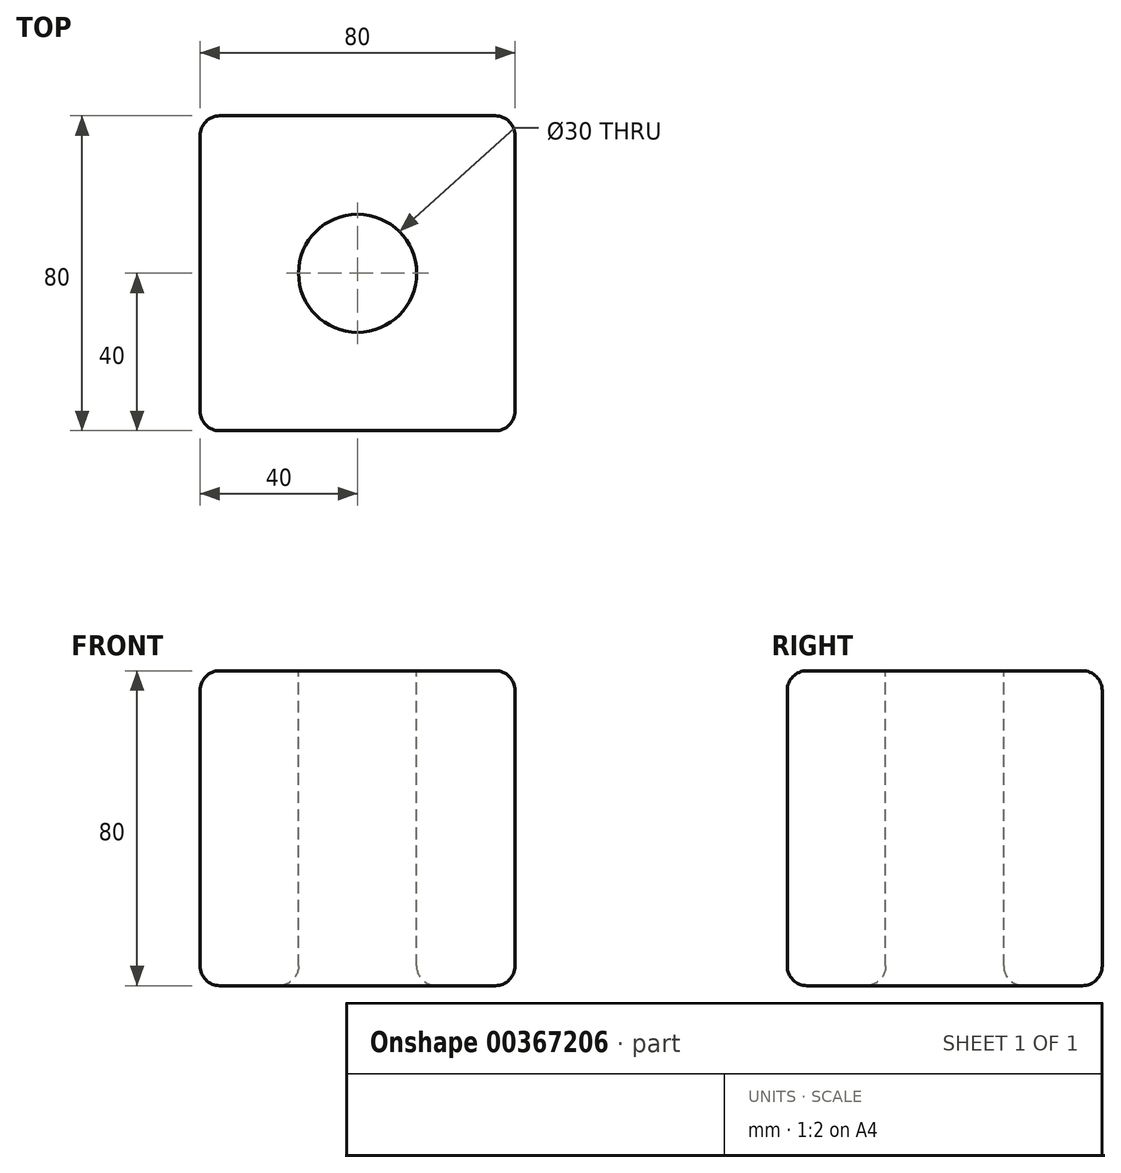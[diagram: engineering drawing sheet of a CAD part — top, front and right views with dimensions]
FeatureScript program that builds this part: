
annotation { "Feature Type Name" : "Feature", "Feature Type Description" : "" }
export const myFeature = defineFeature(function(context is Context, id is Id, definition is map)
    precondition{}
    {
        {
            var Q0;
            Q0=qCreatedBy(makeId("Top.planeOp"),FACE);
            var sketch = newSketch(context, id + "F0", { "sketchPlane" : qUnion([Q0])});
            skLineSegment(sketch, "E0.bottom", {"start": v(-40, 40) * mm, "end": v(40, 40) * mm});
            skLineSegment(sketch, "E0.top", {"start": v(-40, -40) * mm, "end": v(40, -40) * mm});
            skLineSegment(sketch, "E0.left", {"start": v(-40, 40) * mm, "end": v(-40, -40) * mm});
            skLineSegment(sketch, "E0.right", {"start": v(40, 40) * mm, "end": v(40, -40) * mm});
            skPoint(sketch, "E0.middle", {"position": v(0, 0) * mm});
            skSolve(sketch);
        }
        {
            var Q0;
            Q0=makeQuery(id+"F0.imprint","IMPRINT",FACE,{"disambiguationData":[TD([[makeQuery(id+"F0.imprint","IMPRINT",EDGE,{"derivedFrom":sQuery(id+"F0.wireOp",EDGE,"E0.bottom")}),-1.0]])]});
            extrude(context, id + "F1", {"entities" : qUnion([Q0]), "depth" : 80 * mm});
        }
        {
            var Q0;
            Q0=makeQuery(id+"F1.opExtrude","CAP_FACE",FACE,{"disambiguationData":[OSD([sQuery(id+"F0.wireOp",EDGE,"E0.bottom"),sQuery(id+"F0.wireOp",EDGE,"E0.top"),sQuery(id+"F0.wireOp",EDGE,"E0.left"),sQuery(id+"F0.wireOp",EDGE,"E0.right")])],"isStart":false});
            var sketch = newSketch(context, id + "F2", { "sketchPlane" : qUnion([Q0])});
            skCircle(sketch, "E1", {"center": v(0, 0) * mm, "radius": 15 * mm});
            skSolve(sketch);
        }
        {
            var Q0;
            Q0=makeQuery(id+"F2.imprint","IMPRINT",FACE,{"disambiguationData":[TD([[makeQuery(id+"F2.imprint","IMPRINT",EDGE,{"derivedFrom":sQuery(id+"F2.wireOp",EDGE,"E1")}),1.0]])]});
            extrude(context, id + "F3", {"entities" : qUnion([Q0]), "operationType" : NewBodyOperationType.REMOVE, "endBound" : BoundingType.THROUGH_ALL, "oppositeDirection" : true, "depth" : 25 * mm});
        }
        {
            var Q0;
            Q0=makeQuery(id+"F1.opExtrude","SWEPT_EDGE",EDGE,{"disambiguationData":[OSD([sQuery(id+"F0.wireOp",EDGE,"E0.bottom"),sQuery(id+"F0.wireOp",EDGE,"E0.left")])]});
            var Q1;
            Q1=makeQuery(id+"F1.opExtrude","SWEPT_FACE",FACE,{"disambiguationData":[OSD([sQuery(id+"F0.wireOp",EDGE,"E0.bottom")])]});
            var Q2;
            Q2=makeQuery(id+"F1.opExtrude","SWEPT_EDGE",EDGE,{"disambiguationData":[OSD([sQuery(id+"F0.wireOp",EDGE,"E0.bottom"),sQuery(id+"F0.wireOp",EDGE,"E0.right")])]});
            var Q3;
            Q3=makeQuery(id+"F1.opExtrude","SWEPT_FACE",FACE,{"disambiguationData":[OSD([sQuery(id+"F0.wireOp",EDGE,"E0.left")])]});
            var Q4;
            Q4=makeQuery(id+"F1.opExtrude","SWEPT_EDGE",EDGE,{"disambiguationData":[OSD([sQuery(id+"F0.wireOp",EDGE,"E0.top"),sQuery(id+"F0.wireOp",EDGE,"E0.left")])]});
            var Q5;
            Q5=makeQuery(id+"F1.opExtrude","CAP_EDGE",EDGE,{"disambiguationData":[OSD([sQuery(id+"F0.wireOp",EDGE,"E0.left")])],"isStart":false});
            var Q6;
            Q6=makeQuery(id+"F1.opExtrude","CAP_EDGE",EDGE,{"disambiguationData":[OSD([sQuery(id+"F0.wireOp",EDGE,"E0.left")])],"isStart":true});
            var Q7;
            Q7=makeQuery(id+"F1.opExtrude","CAP_EDGE",EDGE,{"disambiguationData":[OSD([sQuery(id+"F0.wireOp",EDGE,"E0.top")])],"isStart":true});
            var Q8;
            Q8=makeQuery(id+"F1.opExtrude","CAP_EDGE",EDGE,{"disambiguationData":[OSD([sQuery(id+"F0.wireOp",EDGE,"E0.right")])],"isStart":true});
            var Q9;
            Q9=makeQuery(id+"F1.opExtrude","CAP_EDGE",EDGE,{"disambiguationData":[OSD([sQuery(id+"F0.wireOp",EDGE,"E0.right")])],"isStart":false});
            var Q10;
            Q10=makeQuery(id+"F1.opExtrude","CAP_EDGE",EDGE,{"disambiguationData":[OSD([sQuery(id+"F0.wireOp",EDGE,"E0.top")])],"isStart":false});
            var Q11;
            Q11=makeQuery(id+"F1.opExtrude","SWEPT_EDGE",EDGE,{"disambiguationData":[OSD([sQuery(id+"F0.wireOp",EDGE,"E0.top"),sQuery(id+"F0.wireOp",EDGE,"E0.right")])]});
            var Q12;
            Q12=makeQuery(id+"F1.opExtrude","CAP_FACE",FACE,{"disambiguationData":[OSD([sQuery(id+"F0.wireOp",EDGE,"E0.bottom"),sQuery(id+"F0.wireOp",EDGE,"E0.top"),sQuery(id+"F0.wireOp",EDGE,"E0.left"),sQuery(id+"F0.wireOp",EDGE,"E0.right")])],"isStart":true});
            fillet(context, id + "F4", {"entities" : qUnion([Q0, Q1, Q2, Q3, Q4, Q5, Q6, Q7, Q8, Q9, Q10, Q11, Q12]), "radius" : 5 * mm, "tangentPropagation" : true, "allowEdgeOverflow" : false});
        }
    });
